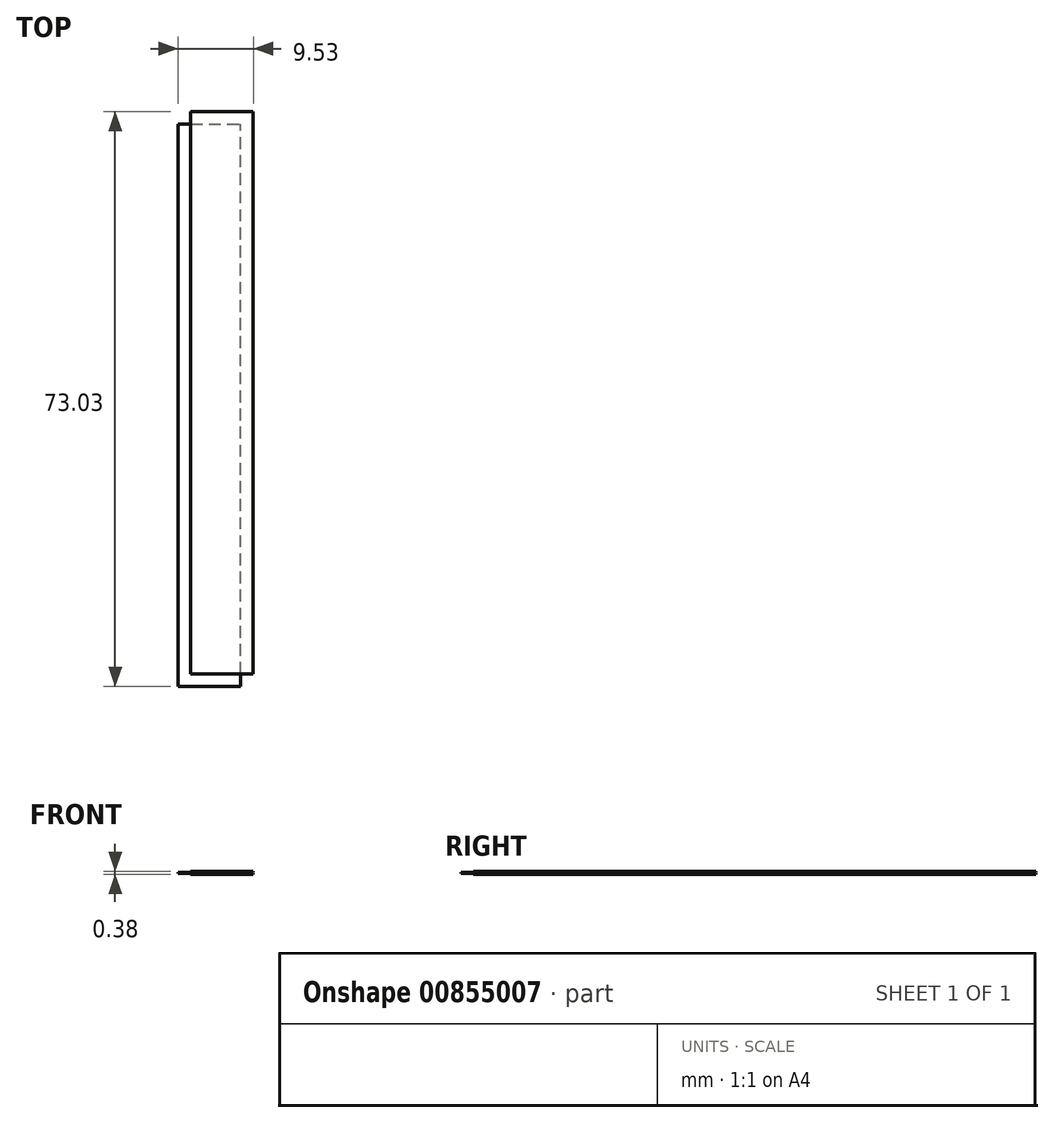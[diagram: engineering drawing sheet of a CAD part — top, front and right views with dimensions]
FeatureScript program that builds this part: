
annotation { "Feature Type Name" : "Feature", "Feature Type Description" : "" }
export const myFeature = defineFeature(function(context is Context, id is Id, definition is map)
    precondition{}
    {
        {
            assignVariable(context, id + "F0", {"name" : "haut", "anyValue" : 3 / 8});
        }
        {
            assignVariable(context, id + "F1", {"name" : "rain_haut", "anyValue" : 1 / 8});
        }
        {
            var Q0;
            Q0=qCreatedBy(makeId("Top.planeOp"),FACE);
            var sketch = newSketch(context, id + "F2", { "sketchPlane" : qUnion([Q0])});
            skLineSegment(sketch, "E0.bottom", {"start": v(0, 0) * mm, "end": v(7.94, 0) * mm});
            skLineSegment(sketch, "E0.top", {"start": v(0, 71.44) * mm, "end": v(7.94, 71.44) * mm});
            skLineSegment(sketch, "E0.left", {"start": v(0, 0) * mm, "end": v(0, 71.44) * mm});
            skLineSegment(sketch, "E0.right", {"start": v(7.94, 0) * mm, "end": v(7.94, 71.44) * mm});
            skSolve(sketch);
        }
        {
            var Q0;
            Q0=qSketchRegion(id+"F2",true);
            extrude(context, id + "F3", {"entities" : qUnion([Q0]), "depth" : ((getVariable(context, 'haut') - getVariable(context, 'rain_haut')) / 2) * mm, "offsetDistance" : 25.4 * mm});
        }
        {
            var Q0;
            Q0=makeQuery(id+"F3.opExtrude","CAP_FACE",FACE,{"disambiguationData":[OSD([sQuery(id+"F2.wireOp",EDGE,"E0.bottom"),sQuery(id+"F2.wireOp",EDGE,"E0.top"),sQuery(id+"F2.wireOp",EDGE,"E0.left"),sQuery(id+"F2.wireOp",EDGE,"E0.right")])],"isStart":false});
            var sketch = newSketch(context, id + "F4", { "sketchPlane" : qUnion([Q0])});
            skLineSegment(sketch, "E1.bottom", {"start": v(-1.59, -1.59) * mm, "end": v(6.35, -1.59) * mm});
            skLineSegment(sketch, "E1.top", {"start": v(-1.59, 69.85) * mm, "end": v(6.35, 69.85) * mm});
            skLineSegment(sketch, "E1.left", {"start": v(-1.59, -1.59) * mm, "end": v(-1.59, 69.85) * mm});
            skLineSegment(sketch, "E1.right", {"start": v(6.35, -1.59) * mm, "end": v(6.35, 69.85) * mm});
            skSolve(sketch);
        }
        {
            var Q0;
            Q0=qSketchRegion(id+"F4",true);
            extrude(context, id + "F5", {"entities" : qUnion([Q0]), "operationType" : NewBodyOperationType.ADD, "depth" : (getVariable(context, 'rain_haut')) * mm, "offsetDistance" : 25.4 * mm});
        }
        {
            var Q0;
            Q0=makeQuery(id+"F5.opExtrude","CAP_FACE",FACE,{"disambiguationData":[OSD([sQuery(id+"F4.wireOp",EDGE,"E1.bottom"),sQuery(id+"F4.wireOp",EDGE,"E1.top"),sQuery(id+"F4.wireOp",EDGE,"E1.left"),sQuery(id+"F4.wireOp",EDGE,"E1.right")])],"isStart":false});
            var sketch = newSketch(context, id + "F6", { "sketchPlane" : qUnion([Q0])});
            skLineSegment(sketch, "E2.bottom", {"start": v(0, 0) * mm, "end": v(7.94, 0) * mm});
            skLineSegment(sketch, "E2.top", {"start": v(0, 71.44) * mm, "end": v(7.94, 71.44) * mm});
            skLineSegment(sketch, "E2.left", {"start": v(0, 0) * mm, "end": v(0, 71.44) * mm});
            skLineSegment(sketch, "E2.right", {"start": v(7.94, 0) * mm, "end": v(7.94, 71.44) * mm});
            skSolve(sketch);
        }
        {
            var Q0;
            Q0=qSketchRegion(id+"F6",true);
            extrude(context, id + "F7", {"entities" : qUnion([Q0]), "operationType" : NewBodyOperationType.ADD, "depth" : ((getVariable(context, 'haut') - getVariable(context, 'rain_haut')) / 2) * mm, "offsetDistance" : 25.4 * mm});
        }
    });
